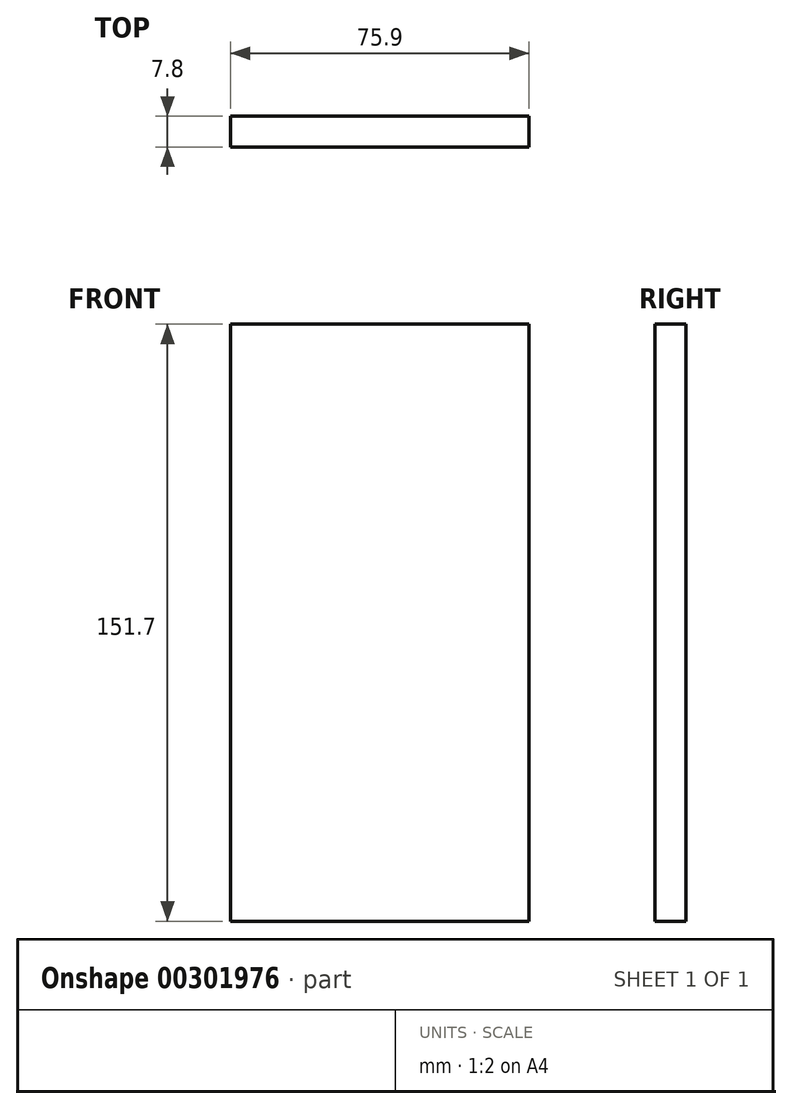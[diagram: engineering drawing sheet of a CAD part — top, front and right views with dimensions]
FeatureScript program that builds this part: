
annotation { "Feature Type Name" : "Feature", "Feature Type Description" : "" }
export const myFeature = defineFeature(function(context is Context, id is Id, definition is map)
    precondition{}
    {
        {
            var Q0;
            Q0=qCreatedBy(makeId("Front.planeOp"),FACE);
            var sketch = newSketch(context, id + "F0", { "sketchPlane" : qUnion([Q0])});
            skLineSegment(sketch, "E0.bottom", {"start": v(37.95, 75.85) * mm, "end": v(-37.95, 75.85) * mm});
            skLineSegment(sketch, "E0.top", {"start": v(37.95, -75.85) * mm, "end": v(-37.95, -75.85) * mm});
            skLineSegment(sketch, "E0.left", {"start": v(37.95, 75.85) * mm, "end": v(37.95, -75.85) * mm});
            skLineSegment(sketch, "E0.right", {"start": v(-37.95, 75.85) * mm, "end": v(-37.95, -75.85) * mm});
            skPoint(sketch, "E0.middle", {"position": v(0, 0) * mm});
            skSolve(sketch);
        }
        {
            var Q0;
            Q0=makeQuery(id+"F0.imprint","IMPRINT",FACE,{"disambiguationData":[TD([[makeQuery(id+"F0.imprint","IMPRINT",EDGE,{"derivedFrom":sQuery(id+"F0.wireOp",EDGE,"E0.bottom")}),1.0]])]});
            extrude(context, id + "F1", {"entities" : qUnion([Q0]), "endBound" : BoundingType.SYMMETRIC, "depth" : 7.8 * mm});
        }
    });
